# Revit family: Go high cabinet
name_source: partatom
category: Furniture
units: mm (PartAtom-declared; Revit-internal decimal feet)

## family parameters
Always vertical = Yes
Cut with Voids When Loaded = No
OmniClass Number = 23.40.20.00
OmniClass Title = General Furniture and Specialties
Room Calculation Point = No
Shared = No
Work Plane-Based = No

## types (3) — shared parameters
Depth cabinet = 350 mm  [stored 1.14829 ft]
Height = 1550 mm  [stored 5.0853 ft]
Manufacturer = Hafa Bathroom Group AB
Material body = Chip board moisture restistant. E1 and FSC certified.
Material front = MDF moisture resistant. E1 and FSC certified.
Model = Go high cabinets
URL = www.hafa.se
Width cabinet = 400 mm  [stored 1.31234 ft]
zero-valued in all types: Material door

## per-type parameters (varying)
| type | Article number | Color | GTIN |
| Go high cabinet white matt | 1580300 | NCS S 0300-N 20% gloss | 7330027103679 |
| Go high cabinet black matt | 1580301 | NCS S 9000-N 10% gloss | 7330027103686 |
| Go high cabinet white gloss | 1580302 | NCS S 0300-N 90% gloss | 7330027101958 |

note: [stored X ft] marks values corroborated as IEEE doubles in the binary element streams (Revit-internal decimal feet)

## geometry (parser evidence)
native form markers: Sweep x2
no freeform markers — native parametric forms only
